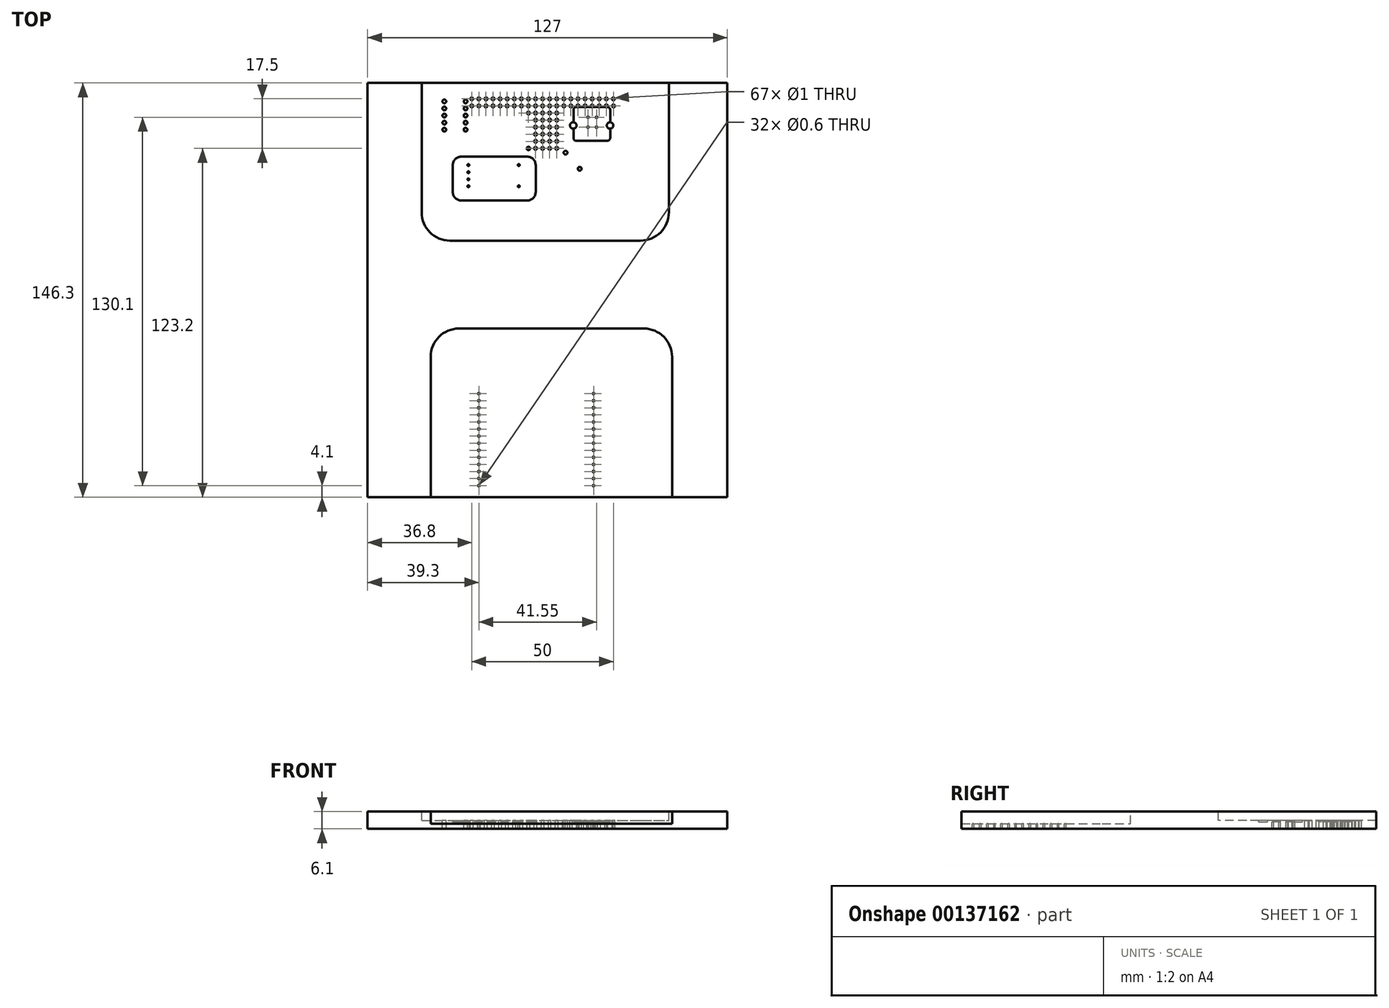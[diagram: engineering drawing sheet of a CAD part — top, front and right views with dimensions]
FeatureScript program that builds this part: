
annotation { "Feature Type Name" : "Feature", "Feature Type Description" : "" }
export const myFeature = defineFeature(function(context is Context, id is Id, definition is map)
    precondition{}
    {
        {
            var Q0;
            Q0=qCreatedBy(makeId("Top.planeOp"),FACE);
            var sketch = newSketch(context, id + "F0", { "sketchPlane" : qUnion([Q0])});
            skLineSegment(sketch, "E0.bottom", {"start": v(-63.5, 73.15) * mm, "end": v(63.5, 73.15) * mm});
            skLineSegment(sketch, "E0.top", {"start": v(-63.5, -73.15) * mm, "end": v(63.5, -73.15) * mm});
            skLineSegment(sketch, "E0.left", {"start": v(-63.5, 73.15) * mm, "end": v(-63.5, -73.15) * mm});
            skLineSegment(sketch, "E0.right", {"start": v(63.5, 73.15) * mm, "end": v(63.5, -73.15) * mm});
            skPoint(sketch, "E0.middle", {"position": v(0, 0) * mm});
            skSolve(sketch);
        }
        {
            var Q0;
            Q0 = qSketchRegion(id + "F0", true);
            extrude(context, id + "F1", {"entities" : qUnion([Q0]), "depth" : 6.1 * mm});
        }
        {
            var Q0;
            Q0=makeQuery(id+"F1.opExtrude","CAP_FACE",FACE,{"disambiguationData":[OSD([sQuery(id+"F0.wireOp",EDGE,"E0.bottom"),sQuery(id+"F0.wireOp",EDGE,"E0.top"),sQuery(id+"F0.wireOp",EDGE,"E0.left"),sQuery(id+"F0.wireOp",EDGE,"E0.right")])],"isStart":false});
            var sketch = newSketch(context, id + "F2", { "sketchPlane" : qUnion([Q0])});
            skLineSegment(sketch, "E1.bottom", {"start": v(-41.2, -73.15) * mm, "end": v(44, -73.15) * mm});
            skLineSegment(sketch, "E1.top", {"start": v(-31.2, -13.55) * mm, "end": v(34, -13.55) * mm});
            skLineSegment(sketch, "E1.left", {"start": v(-41.2, -73.15) * mm, "end": v(-41.2, -23.55) * mm});
            skLineSegment(sketch, "E1.right", {"start": v(44, -73.15) * mm, "end": v(44, -23.55) * mm});
            skPoint(sketch, "E2.visualSharp", {"position": v(-41.2, -13.55) * mm});
            skArc(sketch, "E2.filletArc", {"start": v(-31.2, -13.55) * mm, "mid": v(-38.27, -16.48) * mm, "end": v(-41.2, -23.55) * mm});
            skPoint(sketch, "E3.visualSharp", {"position": v(44, -13.55) * mm});
            skArc(sketch, "E3.filletArc", {"start": v(44, -23.55) * mm, "mid": v(41.07, -16.48) * mm, "end": v(34, -13.55) * mm});
            skSolve(sketch);
        }
        {
            var Q0;
            Q0 = qSketchRegion(id + "F2", true);
            extrude(context, id + "F3", {"entities" : qUnion([Q0]), "operationType" : NewBodyOperationType.REMOVE, "oppositeDirection" : true, "depth" : 4.3 * mm});
        }
        {
            var Q0;
            Q0=makeQuery(id+"F1.opExtrude","CAP_FACE",FACE,{"disambiguationData":[OSD([sQuery(id+"F0.wireOp",EDGE,"E0.bottom"),sQuery(id+"F0.wireOp",EDGE,"E0.top"),sQuery(id+"F0.wireOp",EDGE,"E0.left"),sQuery(id+"F0.wireOp",EDGE,"E0.right")])],"isStart":false});
            var sketch = newSketch(context, id + "F4", { "sketchPlane" : qUnion([Q0])});
            skLineSegment(sketch, "E4.bottom", {"start": v(-44.4, 73.15) * mm, "end": v(42.85, 73.15) * mm});
            skLineSegment(sketch, "E4.top", {"start": v(-34.4, 17.45) * mm, "end": v(32.85, 17.45) * mm});
            skLineSegment(sketch, "E4.left", {"start": v(-44.4, 73.15) * mm, "end": v(-44.4, 27.45) * mm});
            skLineSegment(sketch, "E4.right", {"start": v(42.85, 73.15) * mm, "end": v(42.85, 27.45) * mm});
            skPoint(sketch, "E5.visualSharp", {"position": v(-44.4, 17.45) * mm});
            skArc(sketch, "E5.filletArc", {"start": v(-44.4, 27.45) * mm, "mid": v(-41.47, 20.38) * mm, "end": v(-34.4, 17.45) * mm});
            skPoint(sketch, "E6.visualSharp", {"position": v(42.85, 17.45) * mm});
            skArc(sketch, "E6.filletArc", {"start": v(32.85, 17.45) * mm, "mid": v(39.92, 20.38) * mm, "end": v(42.85, 27.45) * mm});
            skSolve(sketch);
        }
        {
            var Q0;
            Q0 = qSketchRegion(id + "F4", true);
            extrude(context, id + "F5", {"entities" : qUnion([Q0]), "operationType" : NewBodyOperationType.REMOVE, "oppositeDirection" : true, "depth" : 3.1 * mm});
        }
        {
            var Q0;
            Q0=makeQuery(id+"F5.boolean.opBoolean","COPY",FACE,{"derivedFrom":makeQuery(id+"F5.opExtrude","CAP_FACE",FACE,{"disambiguationData":[OSD([sQuery(id+"F4.wireOp",EDGE,"E4.bottom"),sQuery(id+"F4.wireOp",EDGE,"E4.top"),sQuery(id+"F4.wireOp",EDGE,"E4.left"),sQuery(id+"F4.wireOp",EDGE,"E4.right"),sQuery(id+"F4.wireOp",EDGE,"E5.filletArc"),sQuery(id+"F4.wireOp",EDGE,"E6.filletArc")])],"isStart":false})});
            var sketch = newSketch(context, id + "F6", { "sketchPlane" : qUnion([Q0])});
            skCircle(sketch, "E7", {"center": v(-24.2, -36.55) * mm, "radius": 0.3 * mm});
            skCircle(sketch, "E8.0.1.0", {"center": v(-24.2, -39.05) * mm, "radius": 0.3 * mm});
            skCircle(sketch, "E8.0.2.0", {"center": v(-24.2, -41.55) * mm, "radius": 0.3 * mm});
            skCircle(sketch, "E8.0.3.0", {"center": v(-24.2, -44.05) * mm, "radius": 0.3 * mm});
            skCircle(sketch, "E8.0.4.0", {"center": v(-24.2, -46.55) * mm, "radius": 0.3 * mm});
            skCircle(sketch, "E8.0.5.0", {"center": v(-24.2, -49.05) * mm, "radius": 0.3 * mm});
            skCircle(sketch, "E8.0.6.0", {"center": v(-24.2, -51.55) * mm, "radius": 0.3 * mm});
            skCircle(sketch, "E8.0.7.0", {"center": v(-24.2, -54.05) * mm, "radius": 0.3 * mm});
            skCircle(sketch, "E8.0.8.0", {"center": v(-24.2, -56.55) * mm, "radius": 0.3 * mm});
            skCircle(sketch, "E8.0.9.0", {"center": v(-24.2, -59.05) * mm, "radius": 0.3 * mm});
            skCircle(sketch, "E8.0.10.0", {"center": v(-24.2, -61.55) * mm, "radius": 0.3 * mm});
            skCircle(sketch, "E8.0.11.0", {"center": v(-24.2, -64.05) * mm, "radius": 0.3 * mm});
            skCircle(sketch, "E8.0.12.0", {"center": v(-24.2, -66.55) * mm, "radius": 0.3 * mm});
            skCircle(sketch, "E8.0.13.0", {"center": v(-24.2, -69.05) * mm, "radius": 0.3 * mm});
            skCircle(sketch, "E8.1.0.0", {"center": v(16.3, -36.55) * mm, "radius": 0.3 * mm});
            skCircle(sketch, "E8.1.1.0", {"center": v(16.3, -39.05) * mm, "radius": 0.3 * mm});
            skCircle(sketch, "E8.1.2.0", {"center": v(16.3, -41.55) * mm, "radius": 0.3 * mm});
            skCircle(sketch, "E8.1.3.0", {"center": v(16.3, -44.05) * mm, "radius": 0.3 * mm});
            skCircle(sketch, "E8.1.4.0", {"center": v(16.3, -46.55) * mm, "radius": 0.3 * mm});
            skCircle(sketch, "E8.1.5.0", {"center": v(16.3, -49.05) * mm, "radius": 0.3 * mm});
            skCircle(sketch, "E8.1.6.0", {"center": v(16.3, -51.55) * mm, "radius": 0.3 * mm});
            skCircle(sketch, "E8.1.7.0", {"center": v(16.3, -54.05) * mm, "radius": 0.3 * mm});
            skCircle(sketch, "E8.1.8.0", {"center": v(16.3, -56.55) * mm, "radius": 0.3 * mm});
            skCircle(sketch, "E8.1.9.0", {"center": v(16.3, -59.05) * mm, "radius": 0.3 * mm});
            skCircle(sketch, "E8.1.10.0", {"center": v(16.3, -61.55) * mm, "radius": 0.3 * mm});
            skCircle(sketch, "E8.1.11.0", {"center": v(16.3, -64.05) * mm, "radius": 0.3 * mm});
            skCircle(sketch, "E8.1.12.0", {"center": v(16.3, -66.55) * mm, "radius": 0.3 * mm});
            skCircle(sketch, "E8.1.13.0", {"center": v(16.3, -69.05) * mm, "radius": 0.3 * mm});
            skLineSegment(sketch, "E8.direction1", {"start": v(-24.2, -36.55) * mm, "end": v(16.3, -36.55) * mm, "construction": true});
            skLineSegment(sketch, "E8.direction2", {"start": v(-24.2, -36.55) * mm, "end": v(-24.2, -39.05) * mm, "construction": true});
            skCircle(sketch, "E9", {"center": v(-36.4, 66.65) * mm, "radius": 0.65 * mm});
            skCircle(sketch, "E10.0.1.0", {"center": v(-36.4, 64.15) * mm, "radius": 0.65 * mm});
            skCircle(sketch, "E10.0.2.0", {"center": v(-36.4, 61.65) * mm, "radius": 0.65 * mm});
            skCircle(sketch, "E10.0.3.0", {"center": v(-36.4, 59.15) * mm, "radius": 0.65 * mm});
            skCircle(sketch, "E10.0.4.0", {"center": v(-36.4, 56.65) * mm, "radius": 0.65 * mm});
            skCircle(sketch, "E10.1.0.0", {"center": v(-28.9, 66.65) * mm, "radius": 0.65 * mm});
            skCircle(sketch, "E10.1.1.0", {"center": v(-28.9, 64.15) * mm, "radius": 0.65 * mm});
            skCircle(sketch, "E10.1.2.0", {"center": v(-28.9, 61.65) * mm, "radius": 0.65 * mm});
            skCircle(sketch, "E10.1.3.0", {"center": v(-28.9, 59.15) * mm, "radius": 0.65 * mm});
            skCircle(sketch, "E10.1.4.0", {"center": v(-28.9, 56.65) * mm, "radius": 0.65 * mm});
            skLineSegment(sketch, "E10.direction1", {"start": v(-36.4, 66.65) * mm, "end": v(-28.9, 66.65) * mm, "construction": true});
            skLineSegment(sketch, "E10.direction2", {"start": v(-36.4, 66.65) * mm, "end": v(-36.4, 64.15) * mm, "construction": true});
            skCircle(sketch, "E11", {"center": v(-26.7, 67.55) * mm, "radius": 0.5 * mm});
            skCircle(sketch, "E12.0.1.0", {"center": v(-26.7, 65.05) * mm, "radius": 0.5 * mm});
            skCircle(sketch, "E12.1.0.0", {"center": v(-24.2, 67.55) * mm, "radius": 0.5 * mm});
            skCircle(sketch, "E12.1.1.0", {"center": v(-24.2, 65.05) * mm, "radius": 0.5 * mm});
            skCircle(sketch, "E12.2.0.0", {"center": v(-21.7, 67.55) * mm, "radius": 0.5 * mm});
            skCircle(sketch, "E12.2.1.0", {"center": v(-21.7, 65.05) * mm, "radius": 0.5 * mm});
            skCircle(sketch, "E12.3.0.0", {"center": v(-19.2, 67.55) * mm, "radius": 0.5 * mm});
            skCircle(sketch, "E12.3.1.0", {"center": v(-19.2, 65.05) * mm, "radius": 0.5 * mm});
            skCircle(sketch, "E12.4.0.0", {"center": v(-16.7, 67.55) * mm, "radius": 0.5 * mm});
            skCircle(sketch, "E12.4.1.0", {"center": v(-16.7, 65.05) * mm, "radius": 0.5 * mm});
            skCircle(sketch, "E12.5.0.0", {"center": v(-14.2, 67.55) * mm, "radius": 0.5 * mm});
            skCircle(sketch, "E12.5.1.0", {"center": v(-14.2, 65.05) * mm, "radius": 0.5 * mm});
            skCircle(sketch, "E12.6.0.0", {"center": v(-11.7, 67.55) * mm, "radius": 0.5 * mm});
            skCircle(sketch, "E12.6.1.0", {"center": v(-11.7, 65.05) * mm, "radius": 0.5 * mm});
            skCircle(sketch, "E12.7.0.0", {"center": v(-9.2, 67.55) * mm, "radius": 0.5 * mm});
            skCircle(sketch, "E12.7.1.0", {"center": v(-9.2, 65.05) * mm, "radius": 0.5 * mm});
            skCircle(sketch, "E12.8.0.0", {"center": v(-6.7, 67.55) * mm, "radius": 0.5 * mm});
            skCircle(sketch, "E12.8.1.0", {"center": v(-6.7, 65.05) * mm, "radius": 0.5 * mm});
            skCircle(sketch, "E12.9.0.0", {"center": v(-4.2, 67.55) * mm, "radius": 0.5 * mm});
            skCircle(sketch, "E12.9.1.0", {"center": v(-4.2, 65.05) * mm, "radius": 0.5 * mm});
            skCircle(sketch, "E12.10.0.0", {"center": v(-1.7, 67.55) * mm, "radius": 0.5 * mm});
            skCircle(sketch, "E12.10.1.0", {"center": v(-1.7, 65.05) * mm, "radius": 0.5 * mm});
            skCircle(sketch, "E12.11.0.0", {"center": v(0.8, 67.55) * mm, "radius": 0.5 * mm});
            skCircle(sketch, "E12.11.1.0", {"center": v(0.8, 65.05) * mm, "radius": 0.5 * mm});
            skCircle(sketch, "E12.12.0.0", {"center": v(3.3, 67.55) * mm, "radius": 0.5 * mm});
            skCircle(sketch, "E12.12.1.0", {"center": v(3.3, 65.05) * mm, "radius": 0.5 * mm});
            skCircle(sketch, "E12.13.0.0", {"center": v(5.8, 67.55) * mm, "radius": 0.5 * mm});
            skCircle(sketch, "E12.13.1.0", {"center": v(5.8, 65.05) * mm, "radius": 0.5 * mm});
            skCircle(sketch, "E12.14.0.0", {"center": v(8.3, 67.55) * mm, "radius": 0.5 * mm});
            skCircle(sketch, "E12.14.1.0", {"center": v(8.3, 65.05) * mm, "radius": 0.5 * mm});
            skCircle(sketch, "E12.15.0.0", {"center": v(10.8, 67.55) * mm, "radius": 0.5 * mm});
            skCircle(sketch, "E12.15.1.0", {"center": v(10.8, 65.05) * mm, "radius": 0.5 * mm});
            skCircle(sketch, "E12.16.0.0", {"center": v(13.3, 67.55) * mm, "radius": 0.5 * mm});
            skCircle(sketch, "E12.16.1.0", {"center": v(13.3, 65.05) * mm, "radius": 0.5 * mm});
            skCircle(sketch, "E12.17.0.0", {"center": v(15.8, 67.55) * mm, "radius": 0.5 * mm});
            skCircle(sketch, "E12.17.1.0", {"center": v(15.8, 65.05) * mm, "radius": 0.5 * mm});
            skCircle(sketch, "E12.18.0.0", {"center": v(18.3, 67.55) * mm, "radius": 0.5 * mm});
            skCircle(sketch, "E12.18.1.0", {"center": v(18.3, 65.05) * mm, "radius": 0.5 * mm});
            skCircle(sketch, "E12.19.0.0", {"center": v(20.8, 67.55) * mm, "radius": 0.5 * mm});
            skCircle(sketch, "E12.19.1.0", {"center": v(20.8, 65.05) * mm, "radius": 0.5 * mm});
            skCircle(sketch, "E12.20.0.0", {"center": v(23.3, 67.55) * mm, "radius": 0.5 * mm});
            skCircle(sketch, "E12.20.1.0", {"center": v(23.3, 65.05) * mm, "radius": 0.5 * mm});
            skLineSegment(sketch, "E12.direction1", {"start": v(-26.7, 67.55) * mm, "end": v(-24.2, 67.55) * mm, "construction": true});
            skLineSegment(sketch, "E12.direction2", {"start": v(-26.7, 67.55) * mm, "end": v(-26.7, 65.05) * mm, "construction": true});
            skCircle(sketch, "E13", {"center": v(-6.7, 62.55) * mm, "radius": 0.5 * mm});
            skCircle(sketch, "E14", {"center": v(-4.2, 62.55) * mm, "radius": 0.5 * mm});
            skCircle(sketch, "E15.0.1.0", {"center": v(-4.2, 60.05) * mm, "radius": 0.5 * mm});
            skCircle(sketch, "E15.0.2.0", {"center": v(-4.2, 57.55) * mm, "radius": 0.5 * mm});
            skCircle(sketch, "E15.0.3.0", {"center": v(-4.2, 55.05) * mm, "radius": 0.5 * mm});
            skCircle(sketch, "E15.0.4.0", {"center": v(-4.2, 52.55) * mm, "radius": 0.5 * mm});
            skCircle(sketch, "E15.0.5.0", {"center": v(-4.2, 50.05) * mm, "radius": 0.5 * mm});
            skCircle(sketch, "E15.1.0.0", {"center": v(-1.7, 62.55) * mm, "radius": 0.5 * mm});
            skCircle(sketch, "E15.1.1.0", {"center": v(-1.7, 60.05) * mm, "radius": 0.5 * mm});
            skCircle(sketch, "E15.1.2.0", {"center": v(-1.7, 57.55) * mm, "radius": 0.5 * mm});
            skCircle(sketch, "E15.1.3.0", {"center": v(-1.7, 55.05) * mm, "radius": 0.5 * mm});
            skCircle(sketch, "E15.1.4.0", {"center": v(-1.7, 52.55) * mm, "radius": 0.5 * mm});
            skCircle(sketch, "E15.1.5.0", {"center": v(-1.7, 50.05) * mm, "radius": 0.5 * mm});
            skCircle(sketch, "E15.2.0.0", {"center": v(0.8, 62.55) * mm, "radius": 0.5 * mm});
            skCircle(sketch, "E15.2.1.0", {"center": v(0.8, 60.05) * mm, "radius": 0.5 * mm});
            skCircle(sketch, "E15.2.2.0", {"center": v(0.8, 57.55) * mm, "radius": 0.5 * mm});
            skCircle(sketch, "E15.2.3.0", {"center": v(0.8, 55.05) * mm, "radius": 0.5 * mm});
            skCircle(sketch, "E15.2.4.0", {"center": v(0.8, 52.55) * mm, "radius": 0.5 * mm});
            skCircle(sketch, "E15.2.5.0", {"center": v(0.8, 50.05) * mm, "radius": 0.5 * mm});
            skCircle(sketch, "E15.3.0.0", {"center": v(3.3, 62.55) * mm, "radius": 0.5 * mm});
            skCircle(sketch, "E15.3.1.0", {"center": v(3.3, 60.05) * mm, "radius": 0.5 * mm});
            skCircle(sketch, "E15.3.2.0", {"center": v(3.3, 57.55) * mm, "radius": 0.5 * mm});
            skCircle(sketch, "E15.3.3.0", {"center": v(3.3, 55.05) * mm, "radius": 0.5 * mm});
            skCircle(sketch, "E15.3.4.0", {"center": v(3.3, 52.55) * mm, "radius": 0.5 * mm});
            skCircle(sketch, "E15.3.5.0", {"center": v(3.3, 50.05) * mm, "radius": 0.5 * mm});
            skLineSegment(sketch, "E15.direction1", {"start": v(-4.2, 62.55) * mm, "end": v(-1.7, 62.55) * mm, "construction": true});
            skLineSegment(sketch, "E15.direction2", {"start": v(-4.2, 62.55) * mm, "end": v(-4.2, 60.05) * mm, "construction": true});
            skCircle(sketch, "E16", {"center": v(-6.7, 50.05) * mm, "radius": 0.6 * mm});
            skCircle(sketch, "E17", {"center": v(6.4, 48.55) * mm, "radius": 0.66 * mm});
            skCircle(sketch, "E18", {"center": v(11.4, 42.85) * mm, "radius": 0.66 * mm});
            skCircle(sketch, "E19", {"center": v(-27.9, 44.15) * mm, "radius": 0.33 * mm});
            skCircle(sketch, "E20.0.1.0", {"center": v(-27.9, 41.65) * mm, "radius": 0.33 * mm});
            skCircle(sketch, "E20.0.2.0", {"center": v(-27.9, 39.15) * mm, "radius": 0.33 * mm});
            skCircle(sketch, "E20.0.3.0", {"center": v(-27.9, 36.65) * mm, "radius": 0.33 * mm});
            skLineSegment(sketch, "E20.direction2", {"start": v(-27.9, 44.15) * mm, "end": v(-27.9, 41.65) * mm, "construction": true});
            skCircle(sketch, "E21", {"center": v(-10.1, 44.15) * mm, "radius": 0.33 * mm});
            skCircle(sketch, "E22", {"center": v(-10.1, 36.65) * mm, "radius": 0.33 * mm});
            skCircle(sketch, "E23", {"center": v(9.11, 58.15) * mm, "radius": 1.15 * mm});
            skCircle(sketch, "E24", {"center": v(22.11, 58.15) * mm, "radius": 1.15 * mm});
            skCircle(sketch, "E25", {"center": v(17.35, 61.05) * mm, "radius": 0.3 * mm});
            skCircle(sketch, "E26.0.1.0", {"center": v(17.35, 57.55) * mm, "radius": 0.3 * mm});
            skCircle(sketch, "E26.1.0.0", {"center": v(14.35, 61.05) * mm, "radius": 0.3 * mm});
            skCircle(sketch, "E26.1.1.0", {"center": v(14.35, 57.55) * mm, "radius": 0.3 * mm});
            skLineSegment(sketch, "E26.direction1", {"start": v(17.35, 61.05) * mm, "end": v(14.35, 61.05) * mm, "construction": true});
            skLineSegment(sketch, "E26.direction2", {"start": v(17.35, 61.05) * mm, "end": v(17.35, 57.55) * mm, "construction": true});
            skSolve(sketch);
        }
        {
            var Q0;
            Q0 = qSketchRegion(id + "F6", true);
            extrude(context, id + "F7", {"entities" : qUnion([Q0]), "operationType" : NewBodyOperationType.REMOVE, "oppositeDirection" : true, "depth" : 25 * mm});
        }
        {
            var Q0;
            Q0=makeQuery(id+"F5.boolean.opBoolean","COPY",FACE,{"derivedFrom":makeQuery(id+"F5.opExtrude","CAP_FACE",FACE,{"disambiguationData":[OSD([sQuery(id+"F4.wireOp",EDGE,"E4.bottom"),sQuery(id+"F4.wireOp",EDGE,"E4.top"),sQuery(id+"F4.wireOp",EDGE,"E4.left"),sQuery(id+"F4.wireOp",EDGE,"E4.right"),sQuery(id+"F4.wireOp",EDGE,"E5.filletArc"),sQuery(id+"F4.wireOp",EDGE,"E6.filletArc")])],"isStart":false})});
            var sketch = newSketch(context, id + "F8", { "sketchPlane" : qUnion([Q0])});
            skLineSegment(sketch, "E27.bottom", {"start": v(-30.4, 47.15) * mm, "end": v(-7.15, 47.15) * mm});
            skLineSegment(sketch, "E27.top", {"start": v(-30.4, 31.65) * mm, "end": v(-7.15, 31.65) * mm});
            skLineSegment(sketch, "E27.left", {"start": v(-33.4, 44.15) * mm, "end": v(-33.4, 34.65) * mm});
            skLineSegment(sketch, "E27.right", {"start": v(-4.15, 44.15) * mm, "end": v(-4.15, 34.65) * mm});
            skLineSegment(sketch, "E28.bottom", {"start": v(10.2, 64.65) * mm, "end": v(21.15, 64.65) * mm});
            skLineSegment(sketch, "E28.top", {"start": v(10.2, 52.75) * mm, "end": v(21.15, 52.75) * mm});
            skLineSegment(sketch, "E28.left", {"start": v(9.2, 63.65) * mm, "end": v(9.2, 53.75) * mm});
            skLineSegment(sketch, "E28.right", {"start": v(22.15, 63.65) * mm, "end": v(22.15, 53.75) * mm});
            skPoint(sketch, "E29.visualSharp", {"position": v(-33.4, 31.65) * mm});
            skArc(sketch, "E29.filletArc", {"start": v(-33.4, 34.65) * mm, "mid": v(-32.52, 32.53) * mm, "end": v(-30.4, 31.65) * mm});
            skPoint(sketch, "E30.visualSharp", {"position": v(-4.15, 31.65) * mm});
            skArc(sketch, "E30.filletArc", {"start": v(-7.15, 31.65) * mm, "mid": v(-5.03, 32.53) * mm, "end": v(-4.15, 34.65) * mm});
            skPoint(sketch, "E31.visualSharp", {"position": v(-4.15, 47.15) * mm});
            skArc(sketch, "E31.filletArc", {"start": v(-4.15, 44.15) * mm, "mid": v(-5.03, 46.27) * mm, "end": v(-7.15, 47.15) * mm});
            skPoint(sketch, "E32.visualSharp", {"position": v(-33.4, 47.15) * mm});
            skArc(sketch, "E32.filletArc", {"start": v(-30.4, 47.15) * mm, "mid": v(-32.52, 46.27) * mm, "end": v(-33.4, 44.15) * mm});
            skPoint(sketch, "E33.visualSharp", {"position": v(9.2, 52.75) * mm});
            skArc(sketch, "E33.filletArc", {"start": v(9.2, 53.75) * mm, "mid": v(9.5, 53.04) * mm, "end": v(10.2, 52.75) * mm});
            skPoint(sketch, "E34.visualSharp", {"position": v(22.15, 52.75) * mm});
            skArc(sketch, "E34.filletArc", {"start": v(21.15, 52.75) * mm, "mid": v(21.86, 53.04) * mm, "end": v(22.15, 53.75) * mm});
            skPoint(sketch, "E35.visualSharp", {"position": v(9.2, 64.65) * mm});
            skArc(sketch, "E35.filletArc", {"start": v(10.2, 64.65) * mm, "mid": v(9.5, 64.36) * mm, "end": v(9.2, 63.65) * mm});
            skPoint(sketch, "E36.visualSharp", {"position": v(22.15, 64.65) * mm});
            skArc(sketch, "E36.filletArc", {"start": v(22.15, 63.65) * mm, "mid": v(21.86, 64.36) * mm, "end": v(21.15, 64.65) * mm});
            skSolve(sketch);
        }
        {
            var Q0;
            Q0 = qSketchRegion(id + "F8", true);
            extrude(context, id + "F9", {"entities" : qUnion([Q0]), "operationType" : NewBodyOperationType.REMOVE, "oppositeDirection" : true, "depth" : .55 * mm});
        }
    });
